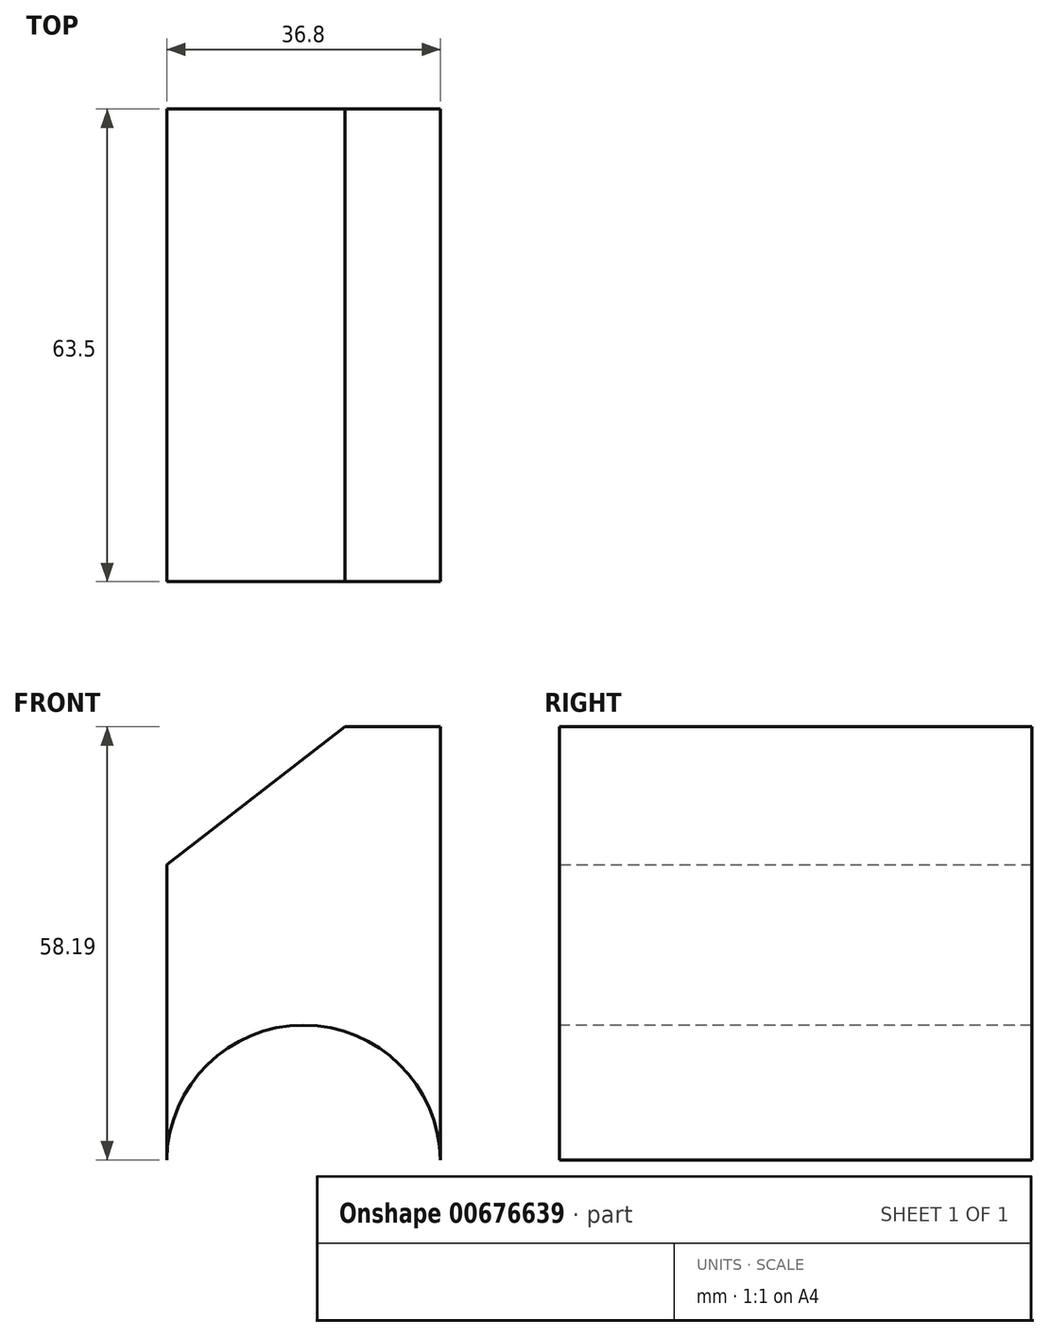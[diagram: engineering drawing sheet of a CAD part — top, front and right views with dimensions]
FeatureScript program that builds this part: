
annotation { "Feature Type Name" : "Feature", "Feature Type Description" : "" }
export const myFeature = defineFeature(function(context is Context, id is Id, definition is map)
    precondition{}
    {
        {
            var Q0;
            Q0=qCreatedBy(makeId("Front.planeOp"),FACE);
            var sketch = newSketch(context, id + "F0", { "sketchPlane" : qUnion([Q0])});
            skLineSegment(sketch, "E0", {"start": v(18.05, -10.07) * mm, "end": v(18.05, 29.61) * mm});
            skLineSegment(sketch, "E1", {"start": v(18.05, 29.61) * mm, "end": v(42, 48.12) * mm});
            skLineSegment(sketch, "E2", {"start": v(42, 48.12) * mm, "end": v(54.85, 48.12) * mm});
            skLineSegment(sketch, "E3", {"start": v(54.85, 48.12) * mm, "end": v(54.85, -10.68) * mm});
            skLineSegment(sketch, "E4", {"start": v(54.85, -10.68) * mm, "end": v(18.05, -10.07) * mm});
            skSolve(sketch);
        }
        {
            var Q0;
            Q0=makeQuery(id+"F0.imprint","IMPRINT",FACE,{"disambiguationData":[TD([[makeQuery(id+"F0.imprint","IMPRINT",EDGE,{"derivedFrom":sQuery(id+"F0.wireOp",EDGE,"E0")}),-1.0]])]});
            extrude(context, id + "F1", {"entities" : qUnion([Q0]), "depth" : 63.5 * mm, "offsetDistance" : 25.4 * mm});
        }
        {
            var Q0;
            Q0=makeQuery(id+"F1.opExtrude","CAP_FACE",FACE,{"disambiguationData":[OSD([sQuery(id+"F0.wireOp",EDGE,"E0"),sQuery(id+"F0.wireOp",EDGE,"E1"),sQuery(id+"F0.wireOp",EDGE,"E2"),sQuery(id+"F0.wireOp",EDGE,"E3"),sQuery(id+"F0.wireOp",EDGE,"E4")])],"isStart":false});
            var sketch = newSketch(context, id + "F2", { "sketchPlane" : qUnion([Q0])});
            skCircle(sketch, "E5", {"center": v(36.45, -10.37) * mm, "radius": 18.4 * mm});
            skSolve(sketch);
        }
        {
            var Q0;
            {var subQ1=makeQuery(id+"F1.opExtrude","CAP_EDGE",EDGE,{"disambiguationData":[OSD([sQuery(id+"F0.wireOp",EDGE,"E4")])],"isStart":false});Q0=makeQuery(id+"F2.imprint","IMPRINT",FACE,{"disambiguationData":[TD([[makeQuery(id+"F2.imprint","IMPRINT",EDGE,{"derivedFrom":subQ1}),-1.0]])]});}
            extrude(context, id + "F3", {"entities" : qUnion([Q0]), "operationType" : NewBodyOperationType.REMOVE, "oppositeDirection" : true, "depth" : 228.6 * mm, "offsetDistance" : 25.4 * mm});
        }
    });
